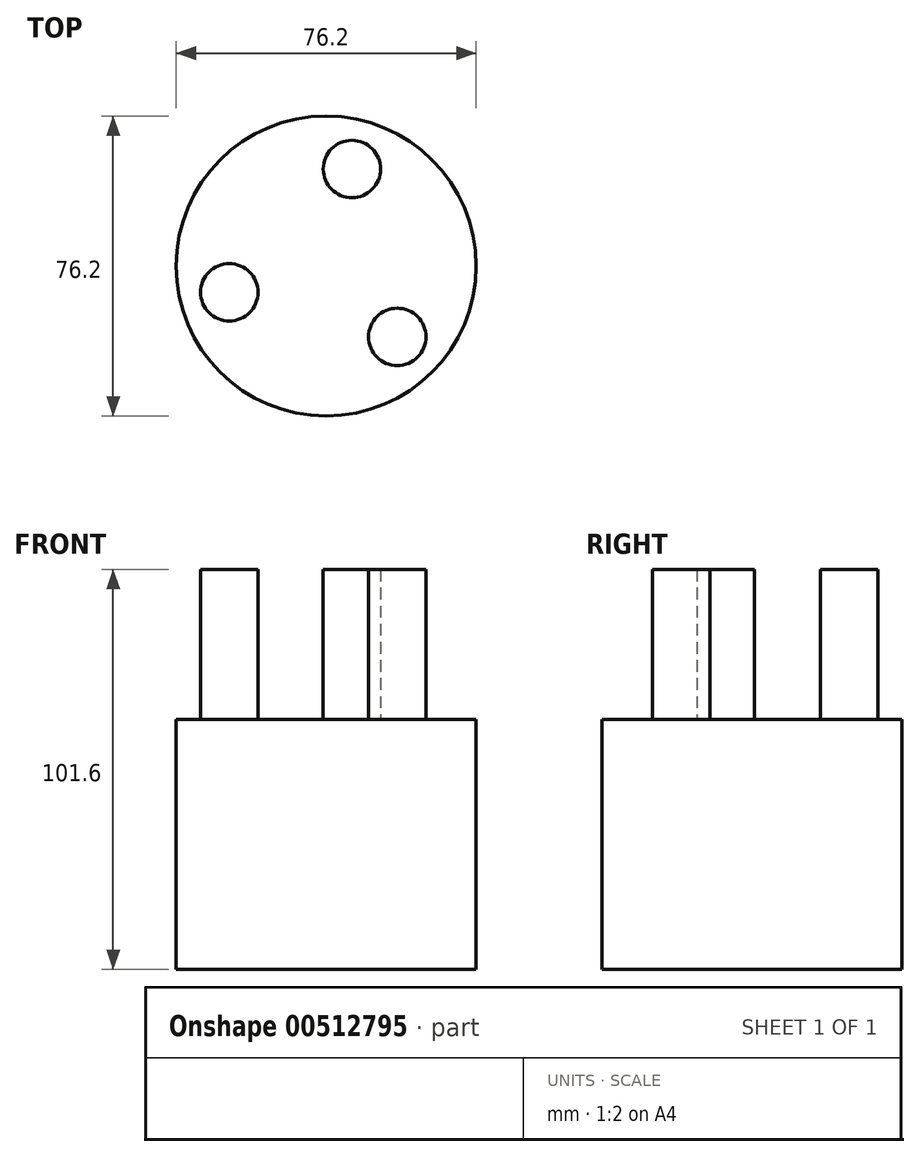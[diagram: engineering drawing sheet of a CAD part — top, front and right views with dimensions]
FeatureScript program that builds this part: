
annotation { "Feature Type Name" : "Feature", "Feature Type Description" : "" }
export const myFeature = defineFeature(function(context is Context, id is Id, definition is map)
    precondition{}
    {
        {
            var Q0;
            Q0=qCreatedBy(makeId("Top.planeOp"),FACE);
            var sketch = newSketch(context, id + "F0", { "sketchPlane" : qUnion([Q0])});
            skCircle(sketch, "E0", {"center": v(0, 0) * mm, "radius": 38.1 * mm});
            skSolve(sketch);
        }
        {
            var Q0;
            Q0=qSketchRegion(id+"F0",true);
            extrude(context, id + "F1", {"entities" : qUnion([Q0]), "depth" : 63.5 * mm});
        }
        {
            var Q0;
            Q0=qCreatedBy(makeId("Top.planeOp"),FACE);
            var sketch = newSketch(context, id + "F2", { "sketchPlane" : qUnion([Q0])});
            skPoint(sketch, "E1.0.midPoint", {"position": v(12.3, 3.33) * mm});
            skCircle(sketch, "E2", {"center": v(6.54, 24.65) * mm, "radius": 7.3 * mm});
            skCircle(sketch, "E3", {"center": v(-24.62, -6.66) * mm, "radius": 7.3 * mm});
            skCircle(sketch, "E4", {"center": v(18.08, -18) * mm, "radius": 7.3 * mm});
            skSolve(sketch);
        }
        {
            var Q0;
            Q0=qSketchRegion(id+"F2",true);
            extrude(context, id + "F3", {"entities" : qUnion([Q0]), "operationType" : NewBodyOperationType.ADD, "depth" : 101.6 * mm});
        }
    });
